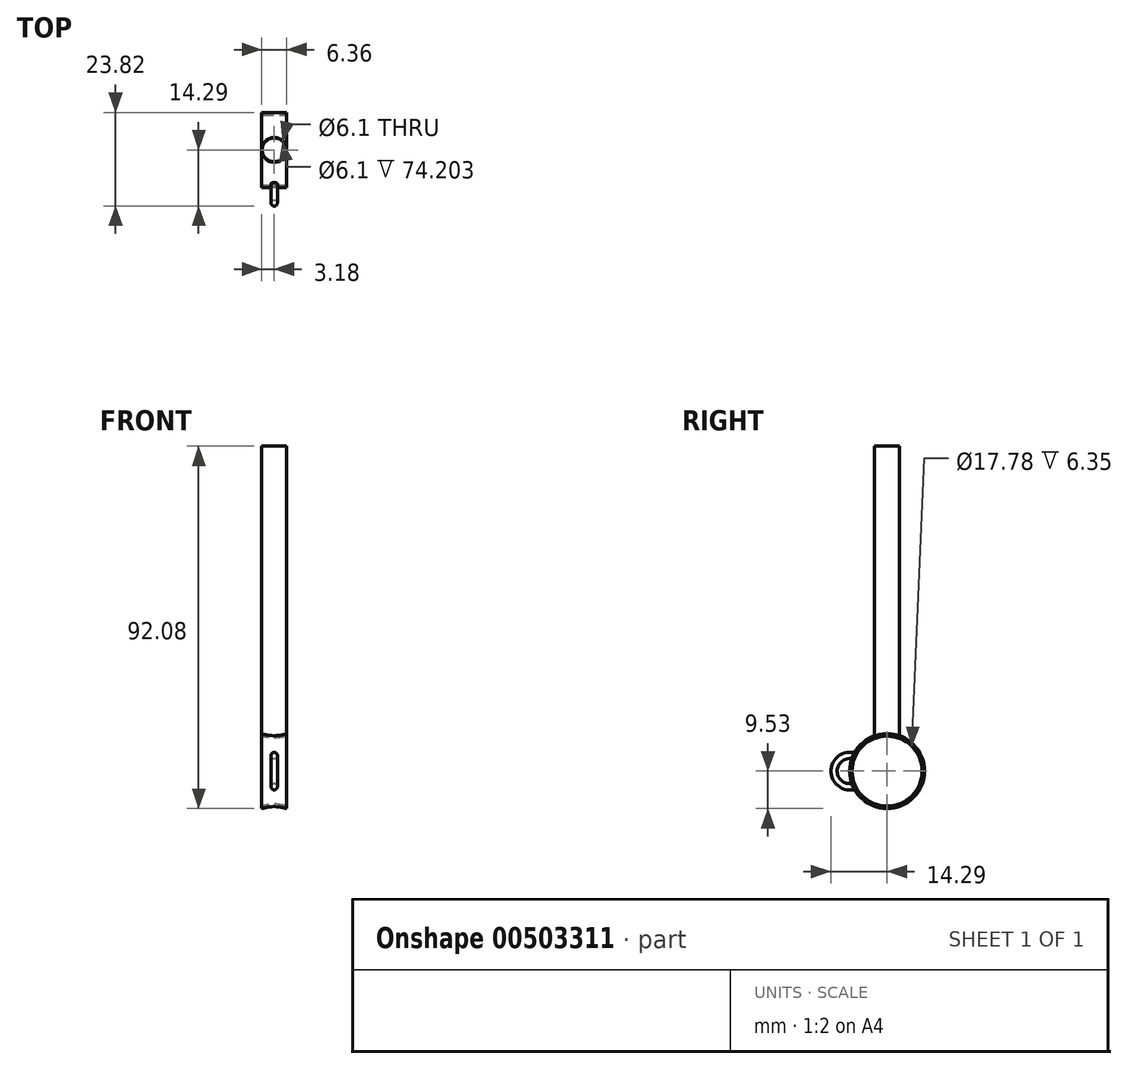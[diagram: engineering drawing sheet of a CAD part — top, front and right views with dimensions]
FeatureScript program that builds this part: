
annotation { "Feature Type Name" : "Feature", "Feature Type Description" : "" }
export const myFeature = defineFeature(function(context is Context, id is Id, definition is map)
    precondition{}
    {
        {
            var Q0;
            Q0=qCreatedBy(makeId("Top.planeOp"),FACE);
            var sketch = newSketch(context, id + "F0", { "sketchPlane" : qUnion([Q0])});
            skCircle(sketch, "E0", {"center": v(0, 0) * mm, "radius": 3.18 * mm});
            skSolve(sketch);
        }
        {
            var Q0;
            Q0=makeQuery(id+"F0.imprint","IMPRINT",FACE,{"disambiguationData":[TD([[makeQuery(id+"F0.imprint","IMPRINT",EDGE,{"derivedFrom":sQuery(id+"F0.wireOp",EDGE,"E0")}),1.0]])]});
            extrude(context, id + "F1", {"entities" : qUnion([Q0]), "endBound" : BoundingType.SYMMETRIC, "depth" : 76.2 * mm});
        }
        {
            var Q0;
            Q0=makeQuery(id+"F1.opExtrude","CAP_FACE",FACE,{"disambiguationData":[OSD([sQuery(id+"F0.wireOp",EDGE,"E0")])],"isStart":true});
            var sketch = newSketch(context, id + "F2", { "sketchPlane" : qUnion([Q0])});
            skCircle(sketch, "E1", {"center": v(0, 0) * mm, "radius": 3.05 * mm});
            skSolve(sketch);
        }
        {
            var Q0;
            Q0=qCreatedBy(makeId("Right.planeOp"),FACE);
            var sketch = newSketch(context, id + "F3", { "sketchPlane" : qUnion([Q0])});
            skCircle(sketch, "E2", {"center": v(0, -44.45) * mm, "radius": 9.53 * mm});
            skSolve(sketch);
        }
        {
            var Q0;
            Q0=makeQuery(id+"F3.imprint","IMPRINT",FACE,{"disambiguationData":[TD([[makeQuery(id+"F3.imprint","IMPRINT",EDGE,{"derivedFrom":sQuery(id+"F3.wireOp",EDGE,"E2")}),1.0]])]});
            extrude(context, id + "F4", {"entities" : qUnion([Q0]), "operationType" : NewBodyOperationType.ADD, "endBound" : BoundingType.SYMMETRIC, "depth" : 6.35 * mm});
        }
        {
            var Q0;
            Q0=makeQuery(id+"F1.opExtrude","CAP_FACE",FACE,{"disambiguationData":[OSD([sQuery(id+"F0.wireOp",EDGE,"E0")])],"isStart":false});
            var sketch = newSketch(context, id + "F5", { "sketchPlane" : qUnion([Q0])});
            skCircle(sketch, "E3", {"center": v(0, 0) * mm, "radius": 3.05 * mm});
            skSolve(sketch);
        }
        {
            var Q0;
            Q0=makeQuery(id+"F5.imprint","IMPRINT",FACE,{"disambiguationData":[TD([[makeQuery(id+"F5.imprint","IMPRINT",EDGE,{"derivedFrom":sQuery(id+"F5.wireOp",EDGE,"E3")}),1.0]])]});
            extrude(context, id + "F6", {"entities" : qUnion([Q0]), "operationType" : NewBodyOperationType.REMOVE, "endBound" : BoundingType.THROUGH_ALL, "oppositeDirection" : true, "depth" : 25.4 * mm});
        }
        {
            var Q0;
            Q0=makeQuery(id+"F4.opExtrude","CAP_FACE",FACE,{"disambiguationData":[OSD([sQuery(id+"F3.wireOp",EDGE,"E2")])],"isStart":false});
            var sketch = newSketch(context, id + "F7", { "sketchPlane" : qUnion([Q0])});
            skCircle(sketch, "E4", {"center": v(0, -44.45) * mm, "radius": 8.9 * mm});
            skSolve(sketch);
        }
        {
            var Q0;
            Q0=makeQuery(id+"F7.imprint","IMPRINT",FACE,{"disambiguationData":[TD([[makeQuery(id+"F7.imprint","IMPRINT",EDGE,{"derivedFrom":sQuery(id+"F7.wireOp",EDGE,"E4")}),1.0]])]});
            extrude(context, id + "F8", {"entities" : qUnion([Q0]), "operationType" : NewBodyOperationType.REMOVE, "endBound" : BoundingType.THROUGH_ALL, "oppositeDirection" : true, "depth" : 25.4 * mm});
        }
        {
            var Q0;
            Q0=qCreatedBy(makeId("Front.planeOp"),FACE);
            cPlane(context, id + "F9", {"entities" : qUnion([Q0]), "cplaneType" : CPlaneType.OFFSET, "offset" : 9.52 * mm, "width" : 152.4 * mm, "height" : 152.4 * mm});
        }
        {
            var Q0;
            Q0=makeQuery(id+"F4.opExtrude","CAP_FACE",FACE,{"disambiguationData":[OSD([sQuery(id+"F3.wireOp",EDGE,"E2")])],"isStart":true});
            var sketch = newSketch(context, id + "F10", { "sketchPlane" : qUnion([Q0])});
            skPoint(sketch, "E5", {"position": v(0, -44.45) * mm});
            skSolve(sketch);
        }
        {
            var Q0;
            Q0=makeQuery(id+"F4.opExtrude","CAP_FACE",FACE,{"disambiguationData":[OSD([sQuery(id+"F3.wireOp",EDGE,"E2")])],"isStart":false});
            var sketch = newSketch(context, id + "F11", { "sketchPlane" : qUnion([Q0])});
            skPoint(sketch, "E6", {"position": v(0, -44.45) * mm});
            skSolve(sketch);
        }
        {
            var Q0;
            Q0=qCreatedBy(id+"F9.planeOp",FACE);
            var sketch = newSketch(context, id + "F12", { "sketchPlane" : qUnion([Q0])});
            skLineSegment(sketch, "E7", {"start": v(-3.18, -44.45) * mm, "end": v(3.18, -44.45) * mm});
            skCircle(sketch, "E8", {"center": v(0, -40.48) * mm, "radius": 0.8 * mm});
            skCircle(sketch, "E9", {"center": v(0, -48.42) * mm, "radius": 0.8 * mm});
            skSolve(sketch);
        }
        {
            var Q0;
            Q0=makeQuery(id+"F12.imprint","IMPRINT",FACE,{"disambiguationData":[TD([[makeQuery(id+"F12.imprint","IMPRINT",EDGE,{"derivedFrom":sQuery(id+"F12.wireOp",EDGE,"E8")}),1.0]])]});
            var Q1;
            Q1=makeQuery(id+"F12.imprint","IMPRINT",FACE,{"disambiguationData":[TD([[makeQuery(id+"F12.imprint","IMPRINT",EDGE,{"derivedFrom":sQuery(id+"F12.wireOp",EDGE,"E9")}),1.0]])]});
            var Q2;
            Q2=makeQuery(id+"F4.opExtrude","SWEPT_FACE",FACE,{"disambiguationData":[OSD([sQuery(id+"F3.wireOp",EDGE,"E2")])]});
            extrude(context, id + "F13", {"entities" : qUnion([Q0, Q1]), "operationType" : NewBodyOperationType.ADD, "endBound" : BoundingType.UP_TO_SURFACE, "oppositeDirection" : true, "endBoundEntityFace" : qUnion([Q2]), "depth" : 25.4 * mm});
        }
        {
            var Q0;
            Q0=makeQuery(id+"F13.opExtrude","CAP_FACE",FACE,{"disambiguationData":[OSD([sQuery(id+"F12.wireOp",EDGE,"E8")])],"isStart":true});
            var sketch = newSketch(context, id + "F14", { "sketchPlane" : qUnion([Q0])});
            skCircle(sketch, "E10.0.0", {"center": v(0, -40.48) * mm, "radius": 0.8 * mm});
            skLineSegment(sketch, "E11", {"start": v(0, -40.48) * mm, "end": v(0, -48.42) * mm});
            skLineSegment(sketch, "E12", {"start": v(0, -44.45) * mm, "end": v(5.44, -44.45) * mm});
            skSolve(sketch);
        }
        {
            var Q0;
            Q0 = qSketchRegion(id + "F14", true);
            var Q1;
            Q1=sQuery(id+"F14.wireOp",EDGE,"E12");
            revolve(context, id + "F15", {"operationType" : NewBodyOperationType.ADD, "entities" : qUnion([Q0]), "axis" : qUnion([Q1]), "revolveType" : RevolveType.ONE_DIRECTION, "angle" : 180 * degree});
        }
    });
